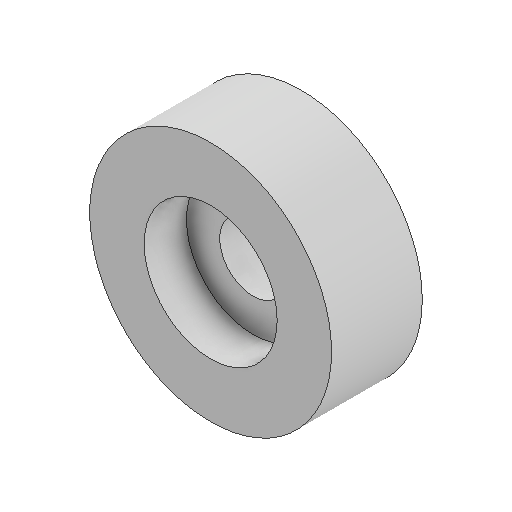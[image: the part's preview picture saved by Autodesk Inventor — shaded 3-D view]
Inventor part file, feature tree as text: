
AUTODESK INVENTOR PART (.ipt)
format: ipt  version: 2025 (Build 290162010, 162A)  size: 114,688 bytes
history: native  units: in
note: dims shown in document units (in); Inventor stores cm internally (conversion verified against a paired STEP export)
features: extrude x2, sketch x1
ambient origin geometry x8: Origin, YZ Plane, XZ Plane, XY Plane, X Axis, Y Axis, Z Axis, Center Point
bodies: Solid1 (feature_tree)
feature tree (3):
  sketch  "Sketch1"  dims[d0=0.22in d1=0.4in d2=0.11in d3=0.08in d4=0.0in d5=0.15in d6=0.0in]
  extrude  "Extrusion1"  Depth=0.15in
  extrude  "Extrusion2"  Depth=0.11in
